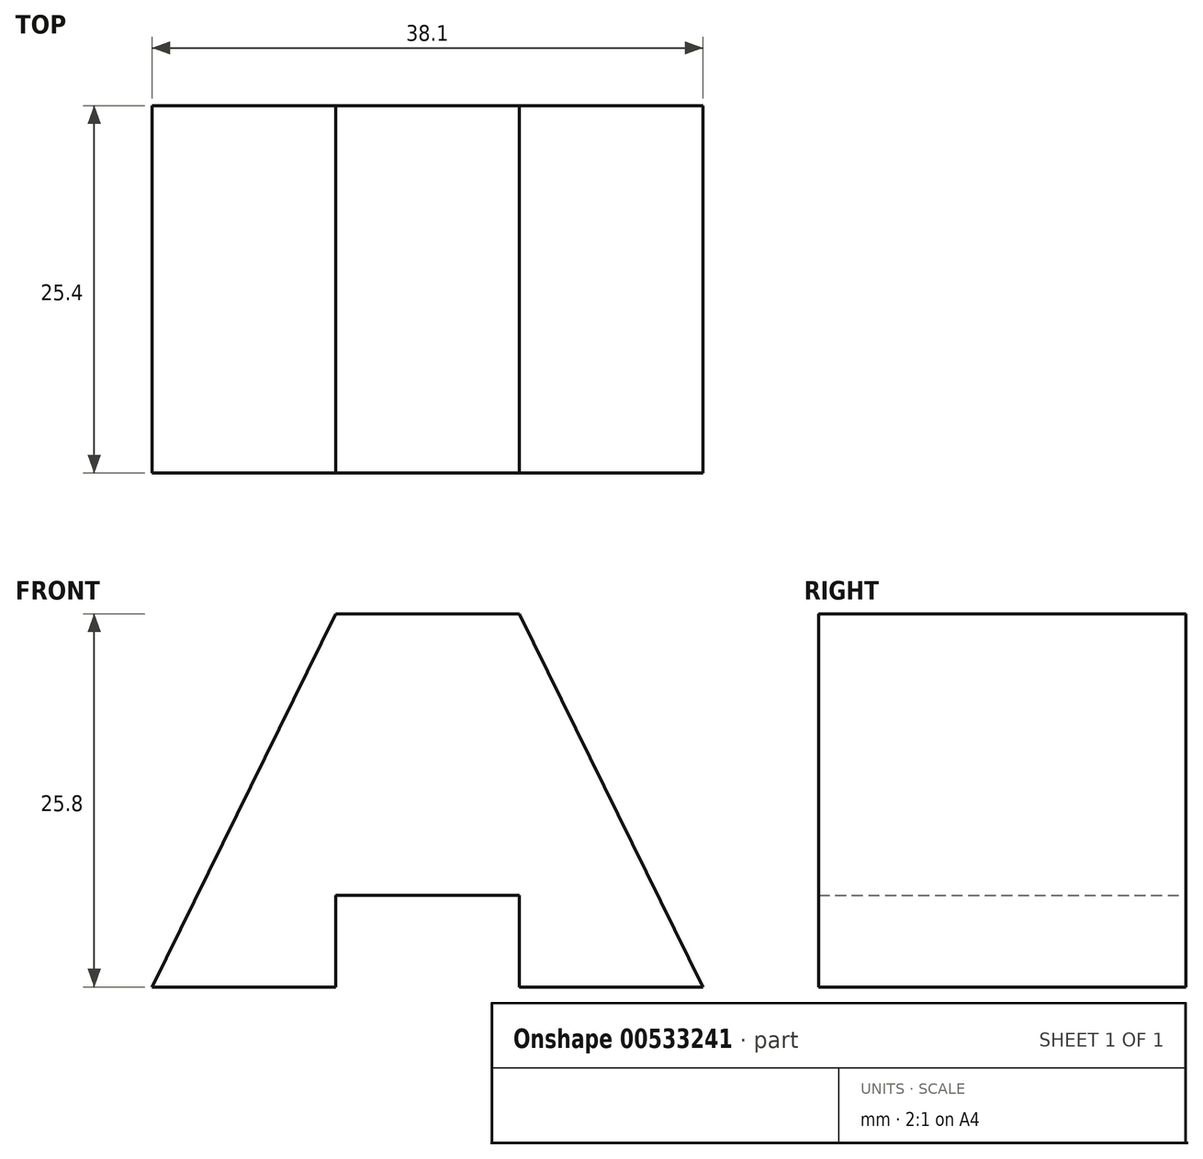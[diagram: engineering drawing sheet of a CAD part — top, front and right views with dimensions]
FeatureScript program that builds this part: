
annotation { "Feature Type Name" : "Feature", "Feature Type Description" : "" }
export const myFeature = defineFeature(function(context is Context, id is Id, definition is map)
    precondition{}
    {
        {
            var Q0;
            Q0=qCreatedBy(makeId("Front.planeOp"),FACE);
            var sketch = newSketch(context, id + "F0", { "sketchPlane" : qUnion([Q0])});
            skLineSegment(sketch, "E0", {"start": v(-54.2, 38.03) * mm, "end": v(-41.5, 38.03) * mm});
            skLineSegment(sketch, "E1", {"start": v(-41.5, 38.03) * mm, "end": v(-28.8, 12.23) * mm});
            skLineSegment(sketch, "E2", {"start": v(-28.8, 12.23) * mm, "end": v(-41.5, 12.23) * mm});
            skLineSegment(sketch, "E3", {"start": v(-41.5, 12.23) * mm, "end": v(-41.5, 18.58) * mm});
            skLineSegment(sketch, "E4", {"start": v(-41.5, 18.58) * mm, "end": v(-54.2, 18.58) * mm});
            skLineSegment(sketch, "E5", {"start": v(-54.2, 18.58) * mm, "end": v(-54.2, 12.23) * mm});
            skLineSegment(sketch, "E6", {"start": v(-54.2, 12.23) * mm, "end": v(-66.9, 12.23) * mm});
            skLineSegment(sketch, "E7", {"start": v(-66.9, 12.23) * mm, "end": v(-54.2, 38.03) * mm});
            skSolve(sketch);
        }
        {
            var Q0;
            Q0=makeQuery(id+"F0.imprint","IMPRINT",FACE,{"disambiguationData":[TD([[makeQuery(id+"F0.imprint","IMPRINT",EDGE,{"derivedFrom":sQuery(id+"F0.wireOp",EDGE,"E0")}),-1.0]])]});
            extrude(context, id + "F1", {"entities" : qUnion([Q0]), "depth" : 25.4 * mm, "offsetDistance" : 25.4 * mm});
        }
    });
